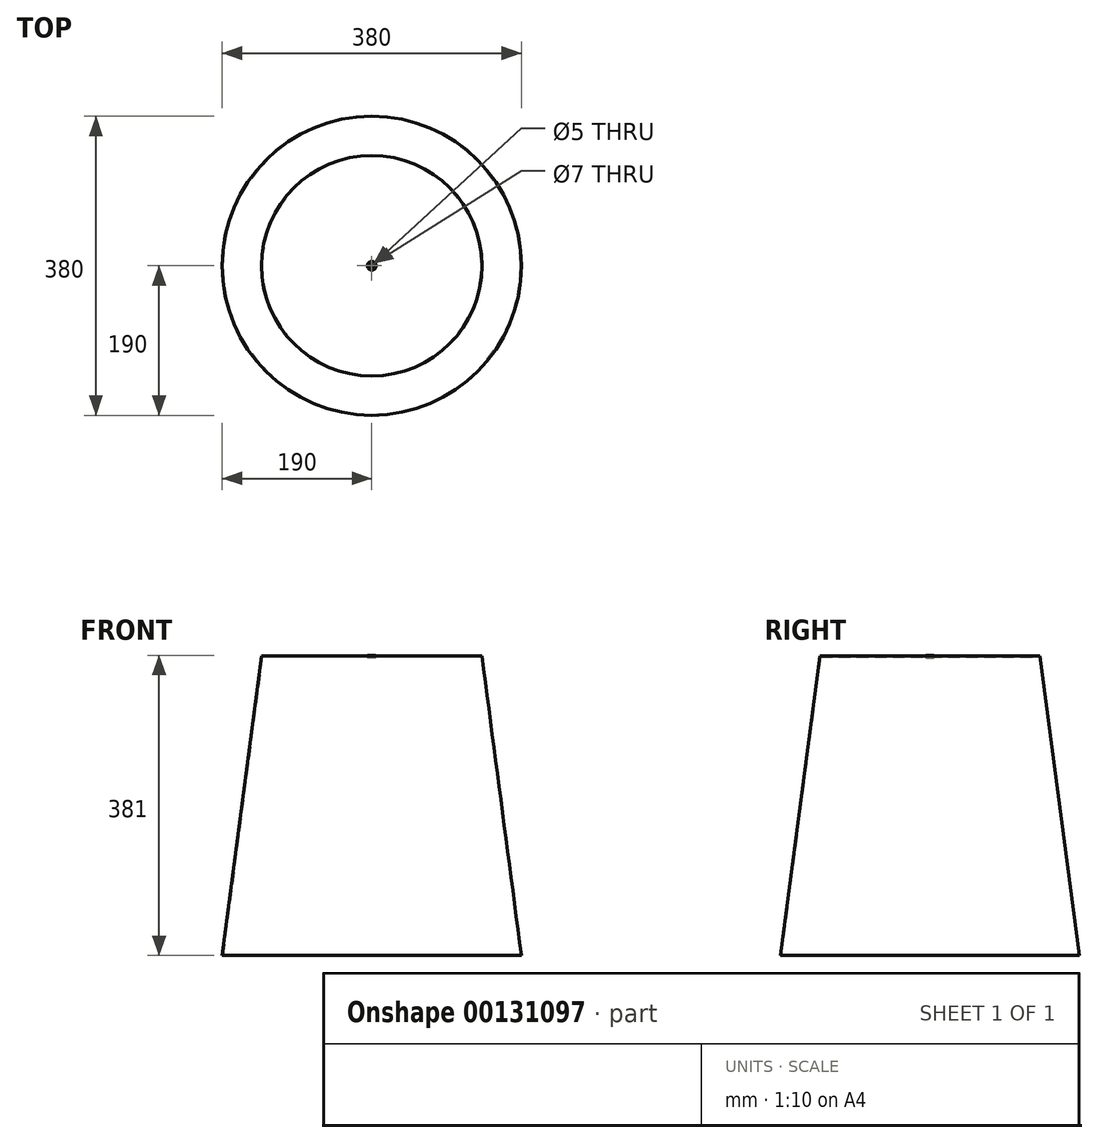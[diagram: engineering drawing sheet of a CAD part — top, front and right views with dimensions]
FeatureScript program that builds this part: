
annotation { "Feature Type Name" : "Feature", "Feature Type Description" : "" }
export const myFeature = defineFeature(function(context is Context, id is Id, definition is map)
    precondition{}
    {
        {
            var Q0;
            Q0=qCreatedBy(makeId("Front.planeOp"),FACE);
            var sketch = newSketch(context, id + "F0", { "sketchPlane" : qUnion([Q0])});
            skLineSegment(sketch, "E0", {"start": v(0, 29.03) * mm, "end": v(0, -50.98) * mm, "construction": true});
            skLineSegment(sketch, "E1", {"start": v(3.5, 380) * mm, "end": v(140, 380) * mm});
            skLineSegment(sketch, "E2", {"start": v(140, 380) * mm, "end": v(190, 0) * mm});
            skLineSegment(sketch, "E3", {"start": v(0, 0) * mm, "end": v(0, 1) * mm});
            skLineSegment(sketch, "E4", {"start": v(189, 0) * mm, "end": v(139.12, 379) * mm});
            skLineSegment(sketch, "E5", {"start": v(139.12, 379) * mm, "end": v(3.5, 379) * mm});
            skLineSegment(sketch, "E6", {"start": v(3.5, 379) * mm, "end": v(3.5, 380) * mm});
            skLineSegment(sketch, "E7", {"start": v(3.5, 380) * mm, "end": v(5.5, 380) * mm});
            skLineSegment(sketch, "E8", {"start": v(5.5, 380) * mm, "end": v(5.5, 381) * mm});
            skLineSegment(sketch, "E9", {"start": v(5.5, 381) * mm, "end": v(2.5, 381) * mm});
            skLineSegment(sketch, "E10", {"start": v(2.5, 381) * mm, "end": v(2.5, 378) * mm});
            skLineSegment(sketch, "E11", {"start": v(2.5, 378) * mm, "end": v(5.5, 378) * mm});
            skLineSegment(sketch, "E12", {"start": v(5.5, 378) * mm, "end": v(5.5, 379) * mm});
            skLineSegment(sketch, "E13", {"start": v(5.5, 379) * mm, "end": v(3.5, 379) * mm});
            skLineSegment(sketch, "E14", {"start": v(190, 0) * mm, "end": v(189, 0) * mm});
            skSolve(sketch);
        }
        {
            var Q0;
            Q0=makeQuery(id+"F0.imprint","IMPRINT",FACE,{"disambiguationData":[TD([[makeQuery(id+"F0.imprint","IMPRINT",EDGE,{"derivedFrom":sQuery(id+"F0.wireOp",EDGE,"E1")}),-1.0]])]});
            var Q1;
            Q1=sQuery(id+"F0.wireOp",EDGE,"E0");
            revolve(context, id + "F1", {"entities" : qUnion([Q0]), "axis" : qUnion([Q1]), "revolveType" : RevolveType.FULL});
        }
        {
            var Q0;
            Q0=makeQuery(id+"F0.imprint","IMPRINT",FACE,{"disambiguationData":[TD([[makeQuery(id+"F0.imprint","IMPRINT",EDGE,{"derivedFrom":sQuery(id+"F0.wireOp",EDGE,"E6")}),1.0]])]});
            var Q1;
            Q1=sQuery(id+"F0.wireOp",EDGE,"E0");
            revolve(context, id + "F2", {"entities" : qUnion([Q0]), "axis" : qUnion([Q1]), "revolveType" : RevolveType.FULL});
        }
        {
            var Q0;
            Q0=makeQuery(id+"F2.opRevolve","SWEPT_EDGE",EDGE,{"disambiguationData":[OSD([sQuery(id+"F0.wireOp",EDGE,"E8"),sQuery(id+"F0.wireOp",EDGE,"E9")])]});
            chamfer(context, id + "F3", {"entities" : qUnion([Q0]), "chamferType" : ChamferType.OFFSET_ANGLE, "width" : 1 * mm, "oppositeDirection" : false, "angle" : 30 * degree, "tangentPropagation" : true});
        }
        {
            var Q0;
            Q0=makeQuery(id+"F2.opRevolve","SWEPT_EDGE",EDGE,{"disambiguationData":[OSD([sQuery(id+"F0.wireOp",EDGE,"E11"),sQuery(id+"F0.wireOp",EDGE,"E12")])]});
            chamfer(context, id + "F4", {"entities" : qUnion([Q0]), "chamferType" : ChamferType.OFFSET_ANGLE, "width" : 1 * mm, "oppositeDirection" : true, "angle" : 30 * degree, "tangentPropagation" : true});
        }
    });
